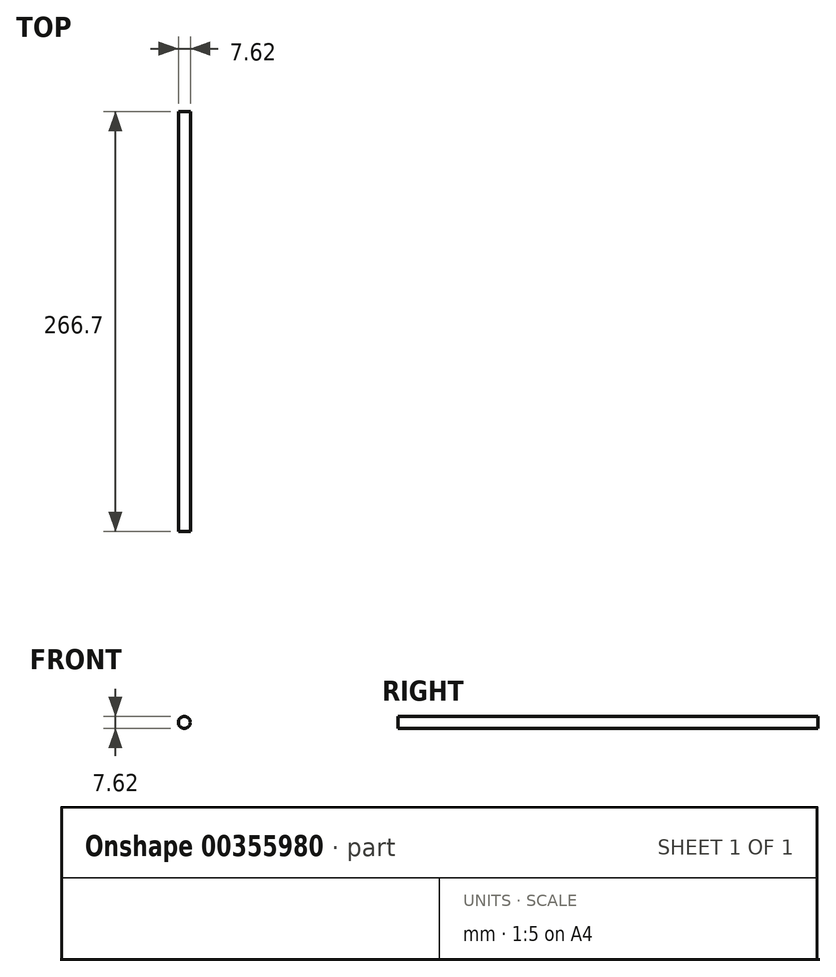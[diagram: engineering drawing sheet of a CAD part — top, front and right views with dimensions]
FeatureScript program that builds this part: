
annotation { "Feature Type Name" : "Feature", "Feature Type Description" : "" }
export const myFeature = defineFeature(function(context is Context, id is Id, definition is map)
    precondition{}
    {
        {
            var Q0;
            Q0=qCreatedBy(makeId("Front.planeOp"),FACE);
            var sketch = newSketch(context, id + "F0", { "sketchPlane" : qUnion([Q0])});
            skCircle(sketch, "E0", {"center": v(0, 0) * mm, "radius": 3.81 * mm});
            skSolve(sketch);
        }
        {
            var Q0;
            Q0=makeQuery(id+"F0.imprint","IMPRINT",FACE,{"disambiguationData":[TD([[makeQuery(id+"F0.imprint","IMPRINT",EDGE,{"derivedFrom":sQuery(id+"F0.wireOp",EDGE,"E0")}),1.0]])]});
            extrude(context, id + "F1", {"entities" : qUnion([Q0]), "depth" : 266.7 * mm});
        }
    });
